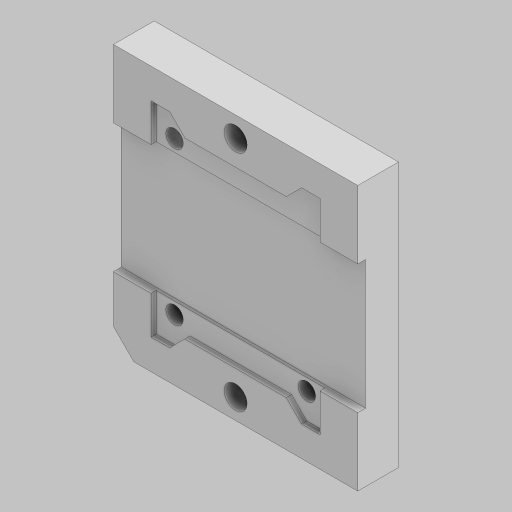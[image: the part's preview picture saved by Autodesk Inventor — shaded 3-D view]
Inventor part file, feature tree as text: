
AUTODESK INVENTOR PART (.ipt)
format: ipt  version: 2023.2 (Build 272271000, 271)  size: 186,368 bytes
history: native  units: in
note: dims shown in document units (in); Inventor stores cm internally (conversion verified against a paired STEP export)
features: reference x10, sketch x5, extrude x3, other x3, hole x2, chamfer x1, thicken_offset x1, projected_geometry x1
ambient origin geometry x8: Origin, YZ Plane, XZ Plane, XY Plane, X Axis, Y Axis, Z Axis, Center Point
bodies: Solid1 (feature_tree)
feature tree (26):
  extrude  "Extrusion1"  Depth=1.8898in
  hole  "Hole1"  [1 undecoded]
  extrude  "Extrusion2"  Depth=0.1339in TaperAngle=0.0deg
  hole  "Hole2"  [1 undecoded]
  chamfer  "Chamfer1"  Distance=0.1575in Angle=45.0deg
  thicken_offset  "Thicken1"
  extrude  "Extrusion3"  Depth=0.9961in
  sketch  "Sketch1"  dims[d0=0.315in d1=0.0in d2=1.8898in]
  sketch  "Sketch2"  dims[d3=2.0472in d4=1.7323in]
  sketch  "Sketch3"  dims[d5=0.1772in d6=0.2362in d7=0.5118in d8=0.1339in d9=90.0deg d10=0.7874in d11=0.0in d12=0.0354in d13=0.0in]
  reference  "Reference1"
  reference  "Reference2"
  reference  "Reference3"
  reference  "Reference4"
  reference  "Reference5"
  reference  "Reference6"
  reference  "Reference7"
  reference  "Reference8"
  reference  "Reference9"
  reference  "Reference10"
  projected_geometry  "Projected Loop1"
  sketch  "Sketch4"  dims[d14=0.0039in d15=0.0039in d16=1.0236in]
  sketch  "Sketch5"  dims[d17=1.1811in d18=0.1339in d19=0.2362in d20=0.2283in d21=0.1339in d22=90.0deg d23=0.315in d24=0.0in d25=0.1575in d26=0.0787in d27=45.0deg d28=0.9961in d29=0.0591in d30=0.0in]
  parser-record x1  (decoder bookkeeping rows leaked as tree rows — omitted from the tree; the rows remain in map.json)
  other  "dsDSLM.iam"
  other  "Chamber_2.0_h_sislicon:1"
note: 2 required parameter values undecoded (feature->parameter linkage not recoverable at this tier; creation-order binding heuristic only, values carry confidence <= 0.55)
note: 1 file-system path scrubbed to <path> (originals preserved in map.json)
